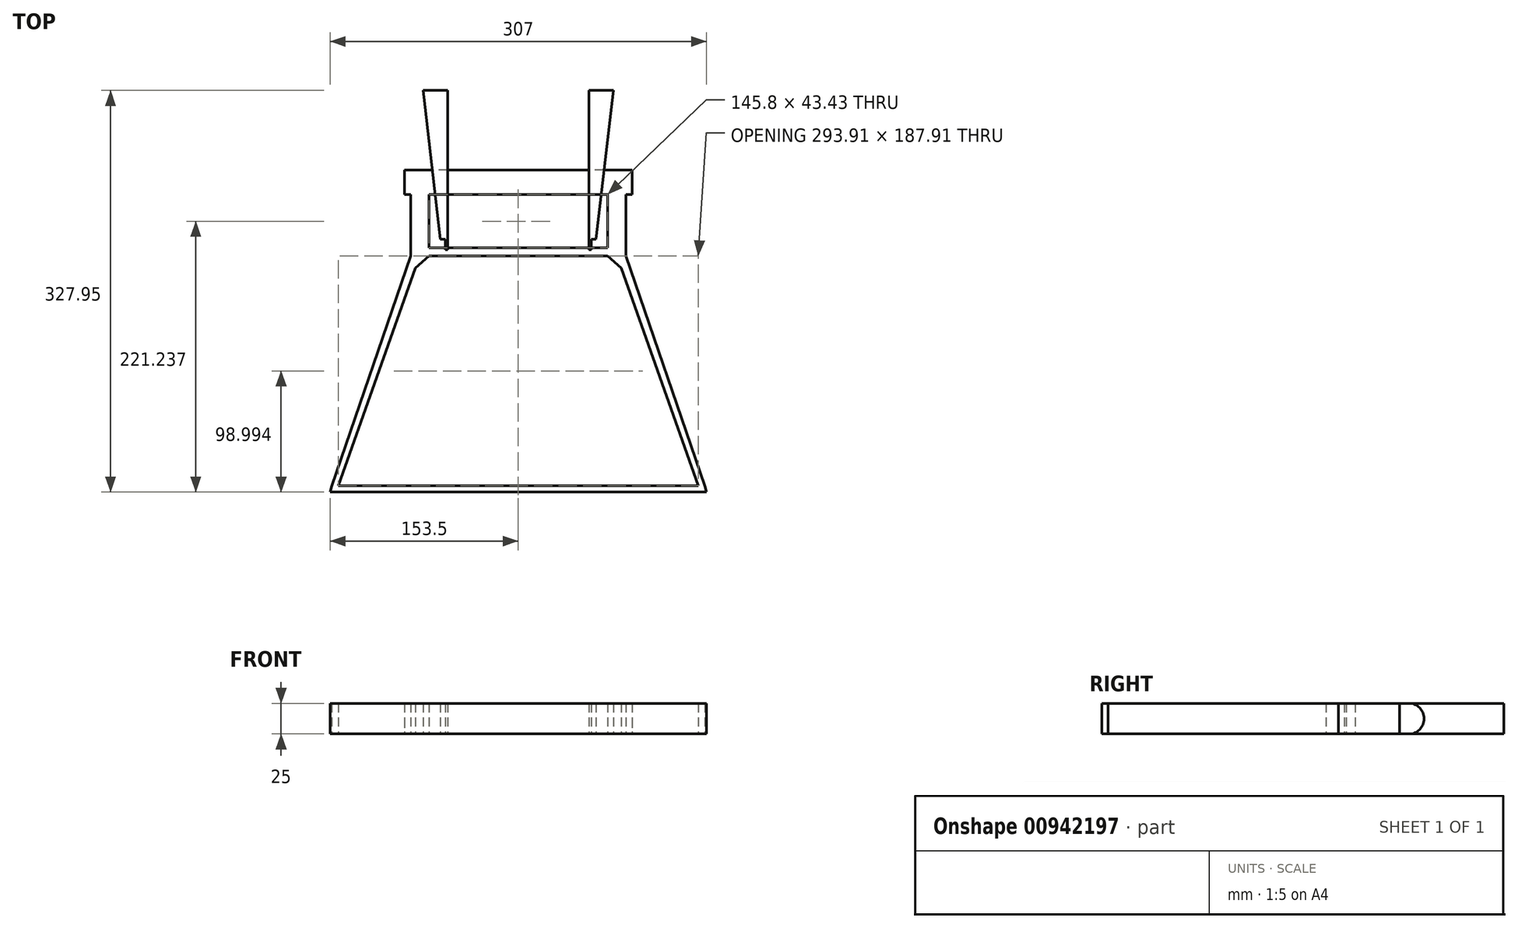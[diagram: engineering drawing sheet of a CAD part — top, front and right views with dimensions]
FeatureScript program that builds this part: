
annotation { "Feature Type Name" : "Feature", "Feature Type Description" : "" }
export const myFeature = defineFeature(function(context is Context, id is Id, definition is map)
    precondition{}
    {
        {
            var Q0;
            Q0=qCreatedBy(makeId("Top.planeOp"),FACE);
            var sketch = newSketch(context, id + "F0", { "sketchPlane" : qUnion([Q0])});
            skLineSegment(sketch, "E0", {"start": v(152.14, -257.94) * mm, "end": v(153.5, -262.95) * mm});
            skLineSegment(sketch, "E1", {"start": v(87.9, -20) * mm, "end": v(87.9, -70) * mm});
            skLineSegment(sketch, "E2", {"start": v(152.14, -257.94) * mm, "end": v(87.9, -70) * mm});
            skLineSegment(sketch, "E3", {"start": v(146.96, -257.91) * mm, "end": v(83.98, -80.11) * mm});
            skLineSegment(sketch, "E4", {"start": v(72.9, -70) * mm, "end": v(72.9, -20) * mm});
            skLineSegment(sketch, "E5", {"start": v(87.9, -20) * mm, "end": v(92.9, -20) * mm});
            skLineSegment(sketch, "E6", {"start": v(92.9, -20) * mm, "end": v(92.9, 0) * mm});
            skLineSegment(sketch, "E7", {"start": v(72.9, -70) * mm, "end": v(83.98, -80.11) * mm});
            skPoint(sketch, "E8.orphan", {"position": v(80.4, -70) * mm});
            skLineSegment(sketch, "E9.MirrorCS", {"start": v(-152.14, -257.94) * mm, "end": v(-87.9, -70) * mm});
            skLineSegment(sketch, "E10.MirrorCS", {"start": v(-146.96, -257.91) * mm, "end": v(-83.98, -80.11) * mm});
            skLineSegment(sketch, "E11.MirrorCS", {"start": v(-72.9, -70) * mm, "end": v(-83.98, -80.11) * mm});
            skLineSegment(sketch, "E12.MirrorCS", {"start": v(-87.9, -20) * mm, "end": v(-87.9, -70) * mm});
            skLineSegment(sketch, "E13.MirrorCS", {"start": v(-152.14, -257.94) * mm, "end": v(-153.5, -262.95) * mm});
            skPoint(sketch, "E14.orphan", {"position": v(-93.24, -70) * mm});
            skPoint(sketch, "E15.MirrorCS.end.orphan", {"position": v(-72.9, -20) * mm});
            skPoint(sketch, "E15.MirrorCS.start.orphan", {"position": v(-72.9, -70) * mm});
            skLineSegment(sketch, "E16.MirrorCS", {"start": v(-72.9, -70) * mm, "end": v(-72.9, -20) * mm});
            skPoint(sketch, "E17.start.orphan", {"position": v(0, 0) * mm});
            skPoint(sketch, "E18.end.orphan", {"position": v(82.5, 0) * mm});
            skPoint(sketch, "E19.start.orphan", {"position": v(87.9, 0) * mm});
            skPoint(sketch, "E20.end.orphan", {"position": v(-82.5, 0) * mm});
            skPoint(sketch, "E21.end.orphan", {"position": v(-88.24, 0) * mm});
            skLineSegment(sketch, "E22", {"start": v(-72.9, -20) * mm, "end": v(72.9, -20) * mm});
            skPoint(sketch, "E23.orphan", {"position": v(-152.14, -257.94) * mm});
            skPoint(sketch, "E24.MirrorCS.end.orphan", {"position": v(-153.5, -262.95) * mm});
            skPoint(sketch, "E25.end.orphan", {"position": v(-3.46, -262.12) * mm});
            skPoint(sketch, "E25.start.orphan", {"position": v(3.46, -262.12) * mm});
            skPoint(sketch, "E26.end.orphan", {"position": v(3.49, -257.12) * mm});
            skPoint(sketch, "E26.start.orphan", {"position": v(-3.49, -257.12) * mm});
            skLineSegment(sketch, "E27", {"start": v(153.5, -262.95) * mm, "end": v(-153.5, -262.95) * mm});
            skLineSegment(sketch, "E28", {"start": v(-146.96, -257.91) * mm, "end": v(146.96, -257.91) * mm});
            skLineSegment(sketch, "E29", {"start": v(92.9, 0) * mm, "end": v(-88.24, 0) * mm});
            skPoint(sketch, "E30.orphan", {"position": v(-93.24, 0) * mm});
            skPoint(sketch, "E31.MirrorCS.end.orphan", {"position": v(-92.9, -20) * mm});
            skPoint(sketch, "E31.MirrorCS.start.orphan", {"position": v(-87.9, -20) * mm});
            skLineSegment(sketch, "E32.MirrorCS", {"start": v(-92.9, -20) * mm, "end": v(-92.9, 0) * mm});
            skLineSegment(sketch, "E33.MirrorCS", {"start": v(-92.9, 0) * mm, "end": v(88.24, 0) * mm});
            skLineSegment(sketch, "E34.MirrorCS", {"start": v(-87.9, -20) * mm, "end": v(-92.9, -20) * mm});
            skLineSegment(sketch, "E35", {"start": v(72.9, -70) * mm, "end": v(-72.9, -70) * mm});
            skLineSegment(sketch, "E36", {"start": v(-72.9, -63.43) * mm, "end": v(72.9, -63.43) * mm});
            skSolve(sketch);
        }
        {
            var Q0;
            Q0 = qSketchRegion(id + "F0", true);
            var Q1;
            {var subQ0=sQuery(id+"F0.wireOp",EDGE,"FTMG4Tsd-k4q1-pfxX-aNJG-cwrck3o0uMLc");Q1=makeQuery(id+"F0.imprint","IMPRINT",FACE,{"disambiguationData":[TD([[makeQuery(id+"F0.imprint","IMPRINT",EDGE,{"derivedFrom":subQ0}),-1.0]])]});}
            var Q2;
            {var subQ0=sQuery(id+"F0.wireOp",EDGE,"E35");Q2=makeQuery(id+"F0.imprint","IMPRINT",FACE,{"disambiguationData":[TD([[makeQuery(id+"F0.imprint","IMPRINT",EDGE,{"derivedFrom":subQ0}),-1.0]])]});}
            extrude(context, id + "F1", {"entities" : qUnion([Q0, Q1, Q2]), "depth" : 25 * mm, "offsetDistance" : 25 * mm});
        }
        {
            var Q0;
            Q0=qCreatedBy(makeId("Top.planeOp"),FACE);
            var sketch = newSketch(context, id + "F2", { "sketchPlane" : qUnion([Q0])});
            skLineSegment(sketch, "E37", {"start": v(-57.5, 0) * mm, "end": v(-57.5, -65) * mm});
            skLineSegment(sketch, "E38", {"start": v(-57.5, 0) * mm, "end": v(-57.5, 65) * mm});
            skLineSegment(sketch, "E39", {"start": v(-57.5, 65) * mm, "end": v(-77.5, 65) * mm});
            skLineSegment(sketch, "E40", {"start": v(-63.5, -56.33) * mm, "end": v(-57.5, -56.33) * mm});
            skLineSegment(sketch, "E41", {"start": v(-63.5, -56.33) * mm, "end": v(-77.5, 65) * mm});
            skLineSegment(sketch, "E42.MirrorCS", {"start": v(57.5, 0) * mm, "end": v(57.5, 65) * mm});
            skLineSegment(sketch, "E43.MirrorCS", {"start": v(57.5, 65) * mm, "end": v(77.5, 65) * mm});
            skLineSegment(sketch, "E44.MirrorCS", {"start": v(63.5, -56.33) * mm, "end": v(77.5, 65) * mm});
            skLineSegment(sketch, "E45.MirrorCS", {"start": v(63.5, -56.33) * mm, "end": v(57.5, -56.33) * mm});
            skLineSegment(sketch, "E46.MirrorCS", {"start": v(57.5, 0) * mm, "end": v(57.5, -65) * mm});
            skLineSegment(sketch, "E47.0", {"start": v(-59.5, 0) * mm, "end": v(-59.5, -65) * mm});
            skLineSegment(sketch, "E48.0", {"start": v(59.5, 0) * mm, "end": v(59.5, -65) * mm});
            skLineSegment(sketch, "E49", {"start": v(-57.5, -65) * mm, "end": v(-59.5, -65) * mm});
            skLineSegment(sketch, "E50", {"start": v(57.5, -65) * mm, "end": v(59.5, -65) * mm});
            skSolve(sketch);
        }
        {
            var Q0;
            Q0 = qSketchRegion(id + "F2", true);
            extrude(context, id + "F3", {"entities" : qUnion([Q0]), "depth" : 25 * mm, "offsetDistance" : 25 * mm});
        }
        {
            var Q0;
            Q0=makeQuery(id+"F1.opExtrude","CAP_EDGE",EDGE,{"disambiguationData":[OSD([sQuery(id+"F0.wireOp",EDGE,"E29"),sQuery(id+"F0.wireOp",EDGE,"E33.MirrorCS")])],"isStart":false});
            var Q1;
            Q1=makeQuery(id+"F1.opExtrude","CAP_EDGE",EDGE,{"disambiguationData":[OSD([sQuery(id+"F0.wireOp",EDGE,"E29"),sQuery(id+"F0.wireOp",EDGE,"E33.MirrorCS")])],"isStart":true});
            fillet(context, id + "F4", {"entities" : qUnion([Q0, Q1]), "radius" : 12.4 * mm, "tangentPropagation" : true, "allowEdgeOverflow" : false});
        }
    });
